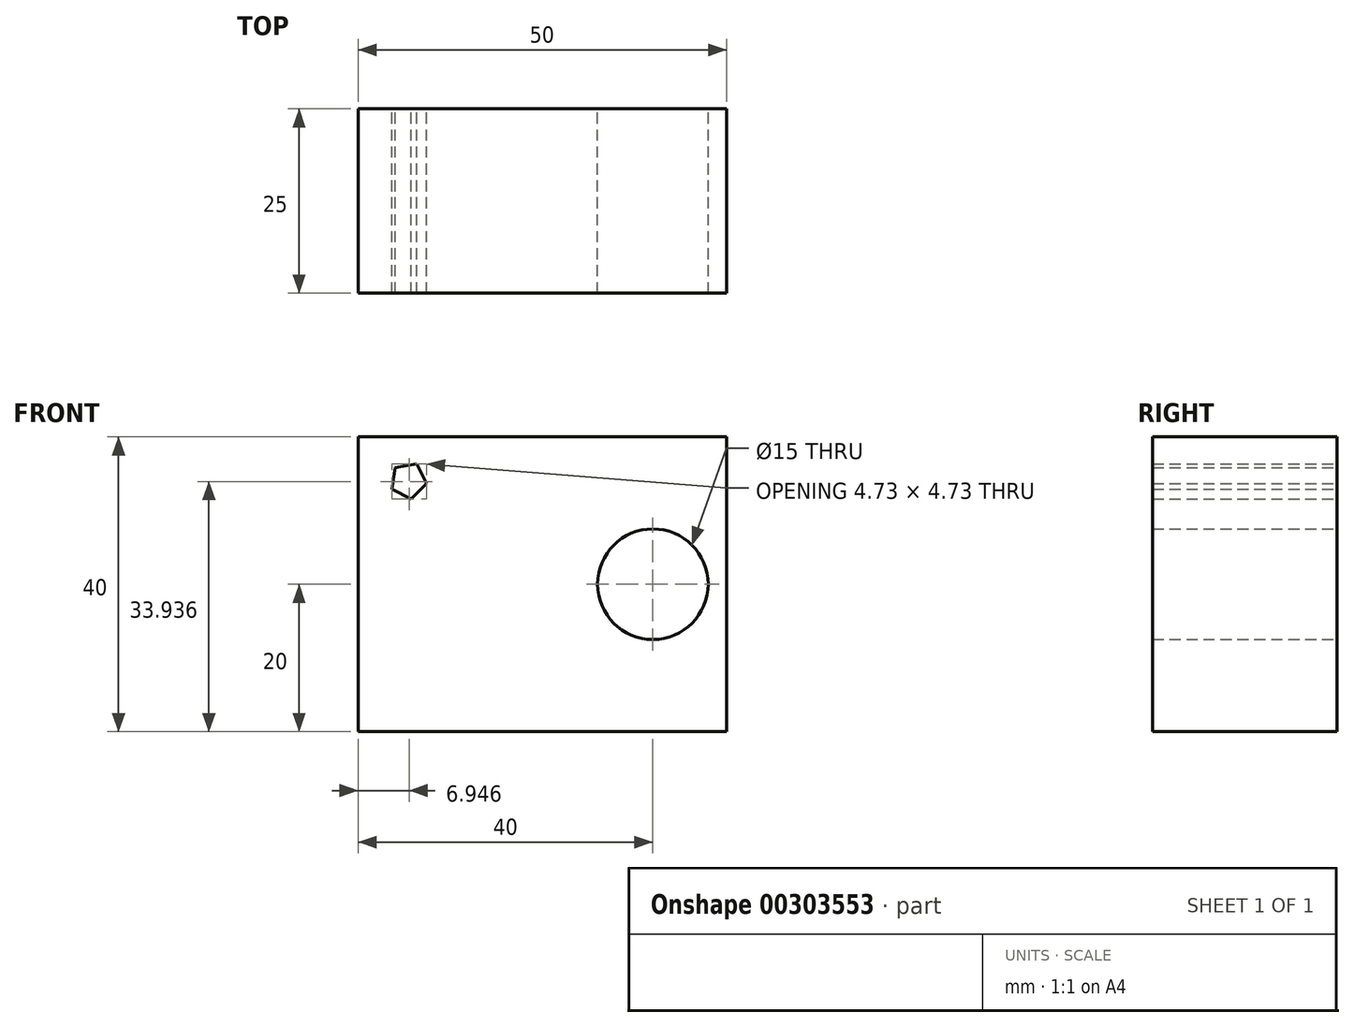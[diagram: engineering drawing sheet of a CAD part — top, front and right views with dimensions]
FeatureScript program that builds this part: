
annotation { "Feature Type Name" : "Feature", "Feature Type Description" : "" }
export const myFeature = defineFeature(function(context is Context, id is Id, definition is map)
    precondition{}
    {
        {
            var Q0;
            Q0=qCreatedBy(makeId("Front.planeOp"),FACE);
            var sketch = newSketch(context, id + "F0", { "sketchPlane" : qUnion([Q0])});
            skLineSegment(sketch, "E0.bottom", {"start": v(0, -20) * mm, "end": v(50, -20) * mm});
            skLineSegment(sketch, "E0.top", {"start": v(0, 20) * mm, "end": v(50, 20) * mm});
            skLineSegment(sketch, "E0.left", {"start": v(0, -20) * mm, "end": v(0, 20) * mm});
            skLineSegment(sketch, "E0.right", {"start": v(50, -20) * mm, "end": v(50, 20) * mm});
            skCircle(sketch, "E1", {"center": v(40, 0) * mm, "radius": 7.5 * mm});
            skPoint(sketch, "E2.center", {"position": v(-0.1, 0.2) * mm});
            skCircle(sketch, "E3.cCircle", {"center": v(6.82, 14.06) * mm, "radius": 2.04 * mm, "construction": true});
            skLineSegment(sketch, "E3.0", {"start": v(9.31, 13.66) * mm, "end": v(7.22, 11.57) * mm});
            skLineSegment(sketch, "E3.1", {"start": v(7.22, 11.57) * mm, "end": v(4.58, 12.91) * mm});
            skLineSegment(sketch, "E3.2", {"start": v(4.58, 12.91) * mm, "end": v(5.04, 15.84) * mm});
            skLineSegment(sketch, "E3.3", {"start": v(5.04, 15.84) * mm, "end": v(7.97, 16.3) * mm});
            skLineSegment(sketch, "E3.4", {"start": v(7.97, 16.3) * mm, "end": v(9.31, 13.66) * mm});
            skPoint(sketch, "E3.0.midPoint", {"position": v(8.27, 12.62) * mm});
            skPoint(sketch, "E4.1.0", {"position": v(-12.92, 8.17) * mm});
            skPoint(sketch, "E4.2.0", {"position": v(-8.47, -13.02) * mm});
            skPoint(sketch, "E4.3.0", {"position": v(12.72, -8.57) * mm});
            skPoint(sketch, "E4.center", {"position": v(-0.1, -0.2) * mm});
            skSolve(sketch);
        }
        {
            var Q0;
            Q0=makeQuery(id+"F0.imprint","IMPRINT",FACE,{"disambiguationData":[TD([[makeQuery(id+"F0.imprint","IMPRINT",EDGE,{"derivedFrom":sQuery(id+"F0.wireOp",EDGE,"E0.bottom")}),1.0]])]});
            extrude(context, id + "F1", {"entities" : qUnion([Q0]), "endBound" : BoundingType.SYMMETRIC, "depth" : 25 * mm});
        }
        {
            var Q0;
            Q0=makeQuery(id+"F1.opExtrude","SWEPT_FACE",FACE,{"disambiguationData":[OSD([sQuery(id+"F0.wireOp",EDGE,"E0.right")])]});
            var sketch = newSketch(context, id + "F2", { "sketchPlane" : qUnion([Q0])});
            skText(sketch, "E5", { "text": "ABC", "fontName": "OpenSans-Regular.ttf"});
            const initialGuessF2  = {"E5": [-0.007, 0.00928, 1, 0, 0.00435]};
            skSetInitialGuess(sketch, initialGuessF2);
            skSolve(sketch);
        }
        {
            var Q0;
            Q0 = qSketchRegion(id + "F2", true);
            extrude(context, id + "F3", {"entities" : qUnion([Q0]), "operationType" : NewBodyOperationType.REMOVE, "endBound" : BoundingType.THROUGH_ALL, "depth" : 20 * mm});
        }
    });
